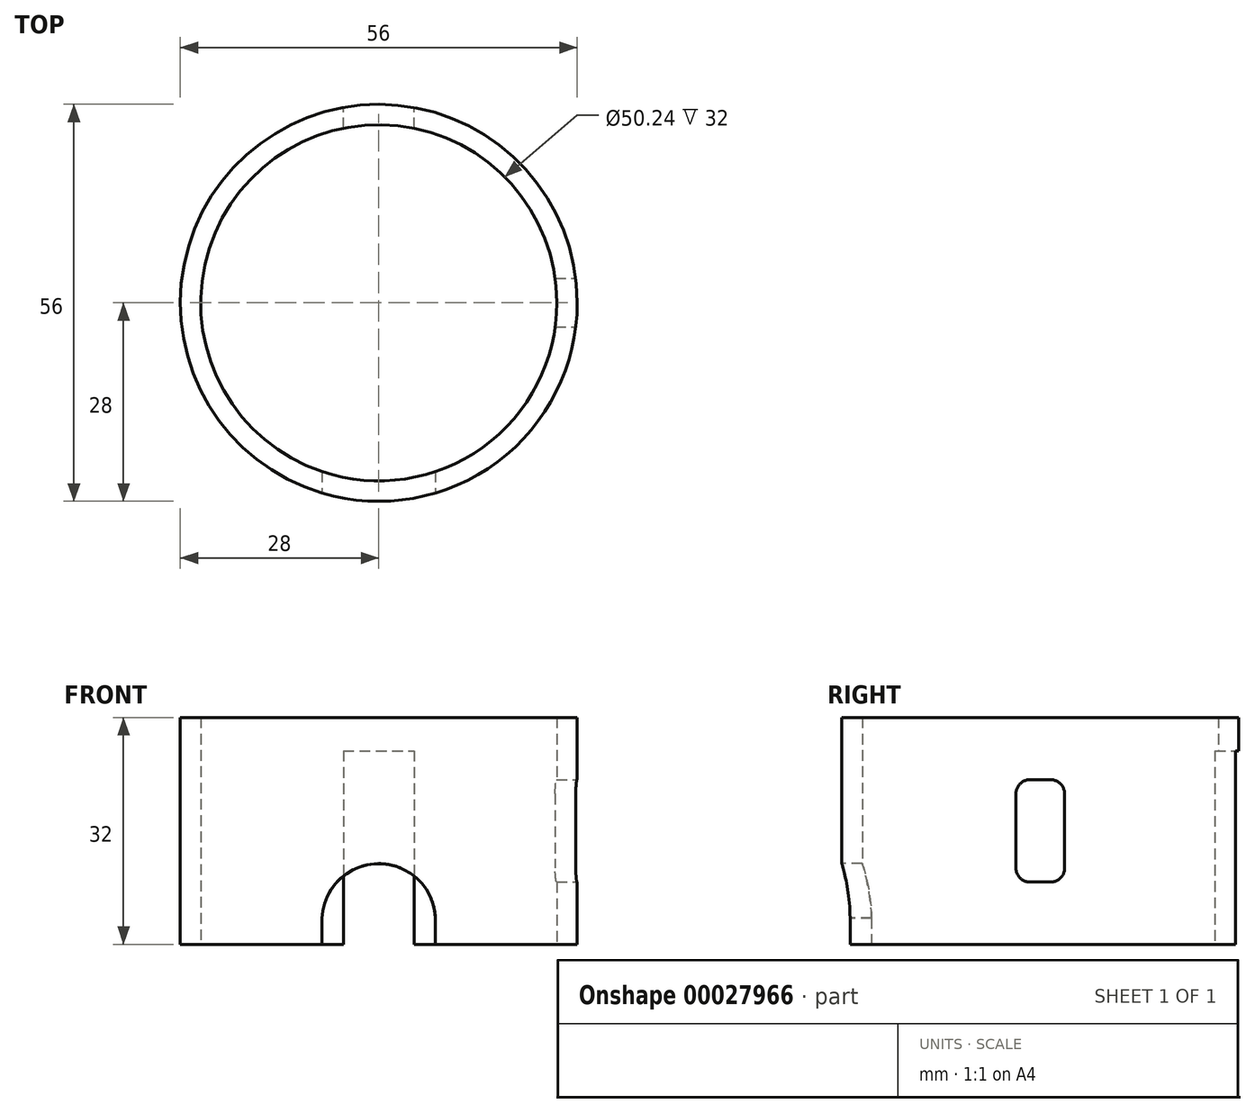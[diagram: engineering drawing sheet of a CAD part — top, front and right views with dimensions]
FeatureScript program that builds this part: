
annotation { "Feature Type Name" : "Feature", "Feature Type Description" : "" }
export const myFeature = defineFeature(function(context is Context, id is Id, definition is map)
    precondition{}
    {
        {
            var Q0;
            Q0=qCreatedBy(makeId("Top.planeOp"),FACE);
            var sketch = newSketch(context, id + "F0", { "sketchPlane" : qUnion([Q0])});
            skCircle(sketch, "E0", {"center": v(0, 0) * mm, "radius": 28 * mm});
            skSolve(sketch);
        }
        {
            var Q0;
            Q0=makeQuery(id+"F0.imprint","IMPRINT",FACE,{"disambiguationData":[TD([[makeQuery(id+"F0.imprint","IMPRINT",EDGE,{"derivedFrom":sQuery(id+"F0.wireOp",EDGE,"E0")}),1.0]])]});
            extrude(context, id + "F1", {"entities" : qUnion([Q0]), "depth" : 32 * mm});
        }
        {
            var Q0;
            Q0=makeQuery(id+"F1.opExtrude","CAP_FACE",FACE,{"disambiguationData":[OSD([sQuery(id+"F0.wireOp",EDGE,"E0")])],"isStart":false});
            var Q1;
            Q1=makeQuery(id+"F1.opExtrude","CAP_FACE",FACE,{"disambiguationData":[OSD([sQuery(id+"F0.wireOp",EDGE,"E0")])],"isStart":true});
            shell(context, id + "F2", {"entities" : qUnion([Q0, Q1]), "thickness" : 2.88 * mm});
        }
        {
            var Q0;
            Q0=qCreatedBy(makeId("Front.planeOp"),FACE);
            cPlane(context, id + "F3", {"entities" : qUnion([Q0]), "cplaneType" : CPlaneType.OFFSET, "offset" : 27.5 * mm, "width" : 150 * mm, "height" : 150 * mm});
        }
        {
            var Q0;
            Q0=qCreatedBy(makeId("Front.planeOp"),FACE);
            cPlane(context, id + "F4", {"entities" : qUnion([Q0]), "cplaneType" : CPlaneType.OFFSET, "offset" : 27.5 * mm, "oppositeDirection" : true, "width" : 150 * mm, "height" : 150 * mm});
        }
        {
            var Q0;
            Q0=qCreatedBy(makeId("Right.planeOp"),FACE);
            cPlane(context, id + "F5", {"entities" : qUnion([Q0]), "cplaneType" : CPlaneType.OFFSET, "offset" : 27.5 * mm, "width" : 150 * mm, "height" : 150 * mm});
        }
        {
            var Q0;
            Q0=qCreatedBy(id+"F3.planeOp",FACE);
            var sketch = newSketch(context, id + "F6", { "sketchPlane" : qUnion([Q0])});
            skLineSegment(sketch, "E1", {"start": v(-28, 0) * mm, "end": v(-28, 32) * mm, "construction": true});
            skLineSegment(sketch, "E2", {"start": v(28, 32) * mm, "end": v(28, 0) * mm, "construction": true});
            skLineSegment(sketch, "E3.0", {"start": v(-28, 32) * mm, "end": v(28, 32) * mm, "construction": true});
            skLineSegment(sketch, "E4.0", {"start": v(-28, 0) * mm, "end": v(28, 0) * mm, "construction": true});
            skLineSegment(sketch, "E5", {"start": v(-28, 16) * mm, "end": v(28, 16) * mm, "construction": true});
            skLineSegment(sketch, "E6", {"start": v(0, 32) * mm, "end": v(0, 0) * mm, "construction": true});
            skArc(sketch, "E7", {"start": v(8, 3.01) * mm, "mid": v(0.04, 11.38) * mm, "end": v(-8, 3.09) * mm});
            skLineSegment(sketch, "E8", {"start": v(-8, 3.67) * mm, "end": v(-8, -6.73) * mm});
            skLineSegment(sketch, "E9", {"start": v(-8, -6.73) * mm, "end": v(8, -6.73) * mm});
            skLineSegment(sketch, "E10", {"start": v(8, 3.75) * mm, "end": v(8, -6.73) * mm});
            skSolve(sketch);
        }
        {
            var Q0;
            Q0=qCreatedBy(id+"F5.planeOp",FACE);
            var sketch = newSketch(context, id + "F7", { "sketchPlane" : qUnion([Q0])});
            skLineSegment(sketch, "E11", {"start": v(28, 32) * mm, "end": v(28, 0) * mm, "construction": true});
            skLineSegment(sketch, "E12.0", {"start": v(-28, 32) * mm, "end": v(28, 32) * mm, "construction": true});
            skLineSegment(sketch, "E13.0", {"start": v(-28, 0) * mm, "end": v(28, 0) * mm, "construction": true});
            skLineSegment(sketch, "E14", {"start": v(-28, 0) * mm, "end": v(-28, 32) * mm, "construction": true});
            skLineSegment(sketch, "E15", {"start": v(-28, 16) * mm, "end": v(28, 16) * mm, "construction": true});
            skLineSegment(sketch, "E16", {"start": v(0, 32) * mm, "end": v(0, 0) * mm, "construction": true});
            skLineSegment(sketch, "E17.bottom", {"start": v(-1.43, 23.23) * mm, "end": v(1.43, 23.23) * mm});
            skLineSegment(sketch, "E17.top", {"start": v(-1.43, 8.77) * mm, "end": v(1.43, 8.77) * mm});
            skLineSegment(sketch, "E17.left", {"start": v(-3.43, 21.23) * mm, "end": v(-3.43, 10.77) * mm});
            skLineSegment(sketch, "E17.right", {"start": v(3.43, 21.23) * mm, "end": v(3.43, 10.77) * mm});
            skPoint(sketch, "E18.visualSharp", {"position": v(-3.43, 23.23) * mm});
            skArc(sketch, "E18.filletArc", {"start": v(-1.43, 23.23) * mm, "mid": v(-2.85, 22.64) * mm, "end": v(-3.43, 21.23) * mm});
            skPoint(sketch, "E19.visualSharp", {"position": v(3.43, 23.23) * mm});
            skArc(sketch, "E19.filletArc", {"start": v(3.43, 21.23) * mm, "mid": v(2.85, 22.64) * mm, "end": v(1.43, 23.23) * mm});
            skPoint(sketch, "E20.visualSharp", {"position": v(3.43, 8.77) * mm});
            skArc(sketch, "E20.filletArc", {"start": v(1.43, 8.77) * mm, "mid": v(2.85, 9.36) * mm, "end": v(3.43, 10.77) * mm});
            skPoint(sketch, "E21.visualSharp", {"position": v(-3.43, 8.77) * mm});
            skArc(sketch, "E21.filletArc", {"start": v(-3.43, 10.77) * mm, "mid": v(-2.85, 9.36) * mm, "end": v(-1.43, 8.77) * mm});
            skSolve(sketch);
        }
        {
            var Q0;
            Q0=makeQuery(id+"F7.imprint","IMPRINT",FACE,{"disambiguationData":[TD([[makeQuery(id+"F7.imprint","IMPRINT",EDGE,{"derivedFrom":sQuery(id+"F7.wireOp",EDGE,"E17.bottom")}),-1.0]])]});
            extrude(context, id + "F8", {"entities" : qUnion([Q0]), "operationType" : NewBodyOperationType.REMOVE, "endBound" : BoundingType.SYMMETRIC, "oppositeDirection" : true, "depth" : 7 * mm});
        }
        {
            var Q0;
            {var subQ1=sQuery(id+"F6.wireOp",EDGE,"E9");Q0=makeQuery(id+"F6.imprint","IMPRINT",FACE,{"disambiguationData":[TD([[makeQuery(id+"F6.imprint","IMPRINT",EDGE,{"derivedFrom":subQ1}),1.0]])]});}
            extrude(context, id + "F9", {"entities" : qUnion([Q0]), "operationType" : NewBodyOperationType.REMOVE, "endBound" : BoundingType.SYMMETRIC, "oppositeDirection" : true, "depth" : 8 * mm});
        }
        {
            var Q0;
            Q0=qCreatedBy(id+"F4.planeOp",FACE);
            var sketch = newSketch(context, id + "F10", { "sketchPlane" : qUnion([Q0])});
            skLineSegment(sketch, "E22.bottom", {"start": v(5, 27.3) * mm, "end": v(-5, 27.3) * mm});
            skLineSegment(sketch, "E22.top", {"start": v(5, -5.06) * mm, "end": v(-5, -5.06) * mm});
            skLineSegment(sketch, "E22.left", {"start": v(5, 27.3) * mm, "end": v(5, -5.06) * mm});
            skLineSegment(sketch, "E22.right", {"start": v(-5, 27.3) * mm, "end": v(-5, -5.06) * mm});
            skLineSegment(sketch, "E23.0", {"start": v(-28, 32) * mm, "end": v(28, 32) * mm});
            skLineSegment(sketch, "E24", {"start": v(0, 32) * mm, "end": v(0, 0) * mm, "construction": true});
            skSolve(sketch);
        }
        {
            var Q0;
            Q0=makeQuery(id+"F10.imprint","IMPRINT",FACE,{"disambiguationData":[TD([[makeQuery(id+"F10.imprint","IMPRINT",EDGE,{"derivedFrom":sQuery(id+"F10.wireOp",EDGE,"E22.bottom")}),1.0]])]});
            extrude(context, id + "F11", {"entities" : qUnion([Q0]), "operationType" : NewBodyOperationType.REMOVE, "endBound" : BoundingType.SYMMETRIC, "depth" : 7 * mm});
        }
    });
